# Revit family: Signage_Plaque_Gemini_Standard-Cast_ISLB
name_source: partatom
category: Generic Models
units: mm (PartAtom-declared; Revit-internal decimal feet)

## family parameters
Always vertical = No
Can host rebar = No
Classification Number = 23.40.90.11.24
Cut with Voids When Loaded = No
Maintain Annotation Orientation = No
Part Type = Normal
Room Calculation Point = No
Round Connector Dimension = Use Diameter
Shared = No
Work Plane-Based = Yes

## types (2) — shared parameters
Assembly Code = E1090900
Border Design = Inset Single Line Bevel
Default Elevation = 0' - 0"
Green Building-LEED = http://www.arcat.com
Keynote = 10400
Manufacturer = Gemini Inc
Manufacturer Fax = 800-421-1256
Manufacturer Website = http://www.geminisignproducts.com
Product Data = http://www.arcat.com
Revision = R1_2015-10
Sales Information = http://www.geminisignproducts.com
Specification = http://www.arcat.com
URL = http://www.geminisignproducts.com
zero-valued in all types: Expected Lifespan (Years), Maintenance Schedule (Months), Warranty Duration (Years)

## per-type parameters (varying)
| type | Description | Frame Material | Model |
| Bronze | Gemini Cast Plaque as Specified - Bronze Inset Single Line Bevel | Metal - Gemini - Bronze | Bronze Inset Single Line Bevel |
| Aluminum | Gemini Cast Plaque as Specified - Aluminum Inset Single Line Bevel | Metal - Gemini - Aluminum | Aluminum Inset Single Line Bevel |

## geometry (parser evidence)
native form markers: Blend x2, Sweep x5
no freeform markers — native parametric forms only
